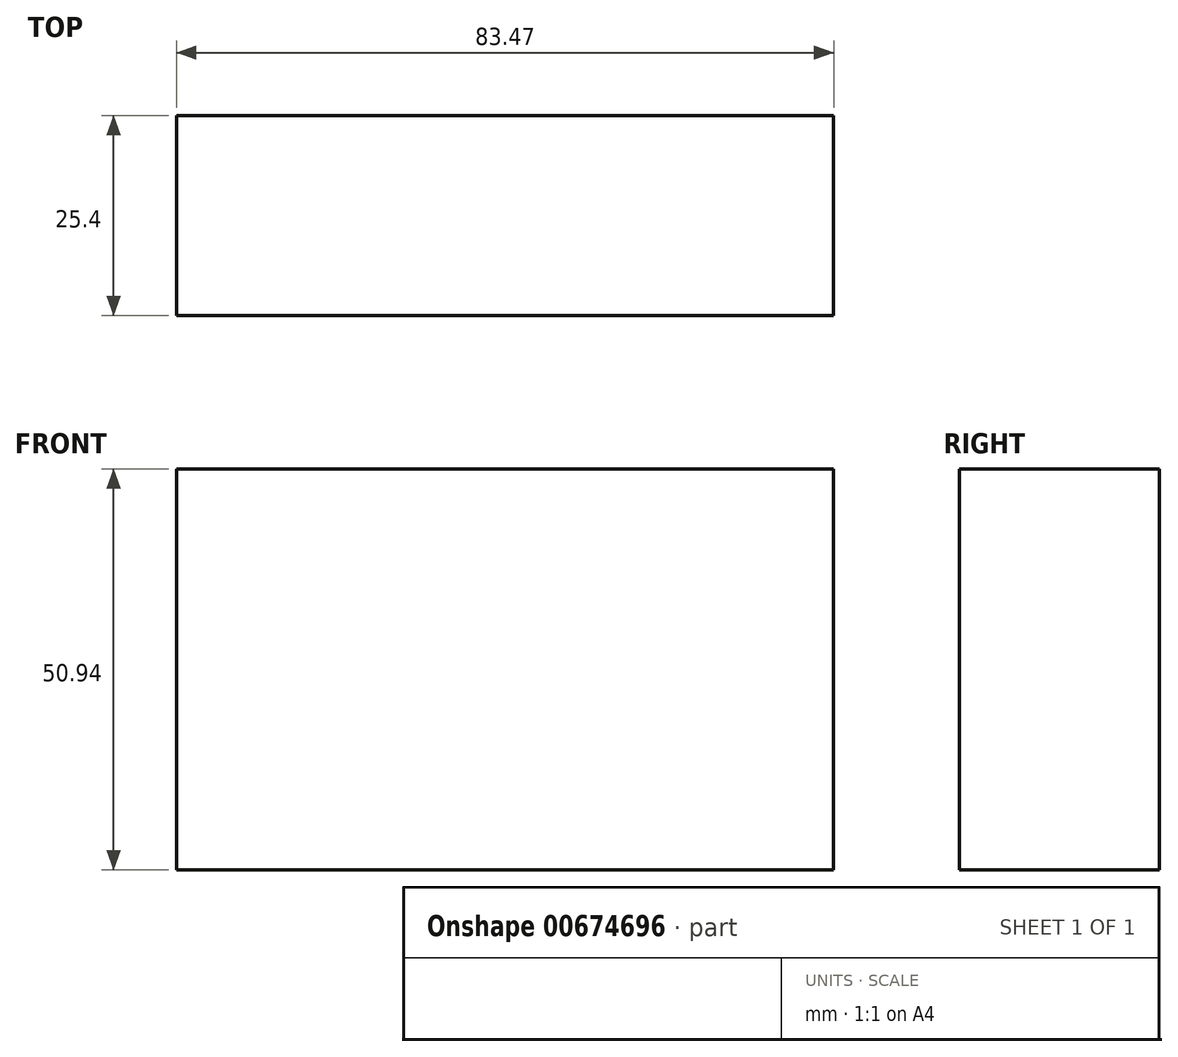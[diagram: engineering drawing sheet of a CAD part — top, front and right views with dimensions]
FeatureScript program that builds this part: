
annotation { "Feature Type Name" : "Feature", "Feature Type Description" : "" }
export const myFeature = defineFeature(function(context is Context, id is Id, definition is map)
    precondition{}
    {
        {
            var Q0;
            Q0=qCreatedBy(makeId("Front.planeOp"),FACE);
            var sketch = newSketch(context, id + "F0", { "sketchPlane" : qUnion([Q0])});
            skLineSegment(sketch, "E0.top", {"start": v(-41.88, -28.92) * mm, "end": v(41.59, -28.92) * mm});
            skLineSegment(sketch, "E0.left", {"start": v(-41.88, 22.02) * mm, "end": v(-41.88, -28.92) * mm});
            skLineSegment(sketch, "E0.right", {"start": v(41.59, 22.02) * mm, "end": v(41.59, -28.92) * mm});
            skLineSegment(sketch, "E1", {"start": v(-41.88, 22.02) * mm, "end": v(41.59, 22.02) * mm});
            skSolve(sketch);
        }
        {
            var Q0;
            Q0=makeQuery(id+"F0.imprint","IMPRINT",FACE,{"disambiguationData":[TD([[makeQuery(id+"F0.imprint","IMPRINT",EDGE,{"derivedFrom":sQuery(id+"F0.wireOp",EDGE,"E0.top")}),1.0]])]});
            extrude(context, id + "F1", {"entities" : qUnion([Q0]), "depth" : 25.4 * mm, "offsetDistance" : 25.4 * mm});
        }
    });
